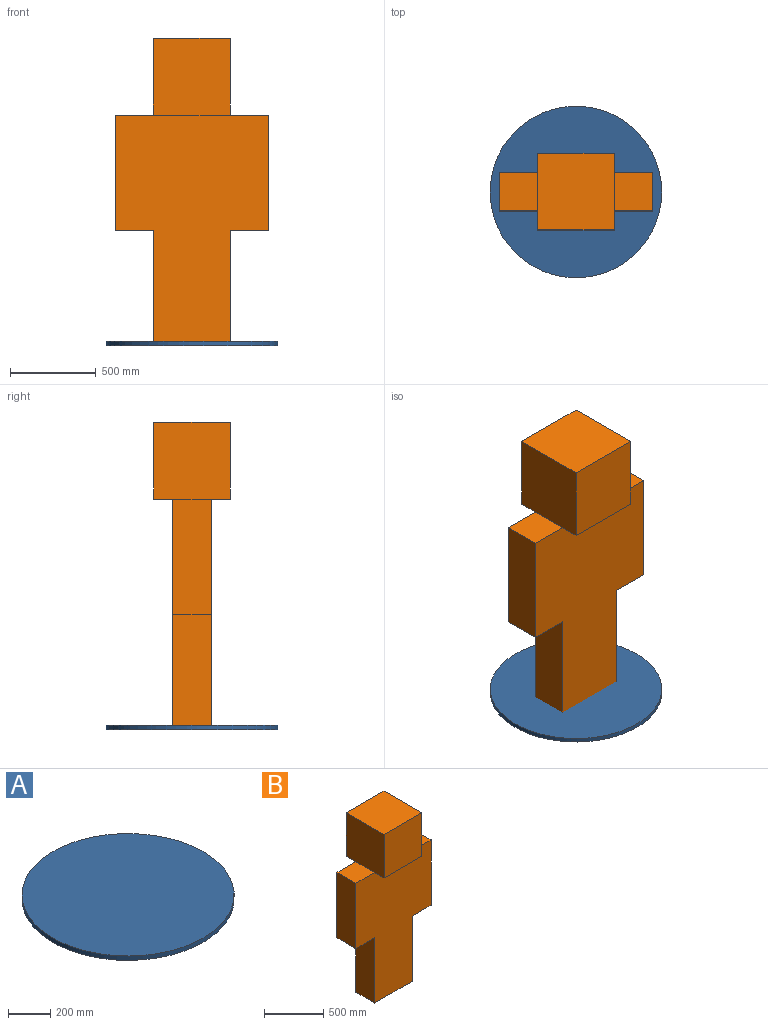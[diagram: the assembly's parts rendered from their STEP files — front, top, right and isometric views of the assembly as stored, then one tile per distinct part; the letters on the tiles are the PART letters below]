
ASSEMBLY  parts=2 mates=1
PART A: 3 faces, bbox 1000x1000x25 mm
  f0: cylinder r=500mm len=1000mm, axis (0,0,-1), area 78539.8mm2, adj f1,f2
  f1: plane 1000x1000mm, normal (0,0,1), area 785398.2mm2, adj f0
  f2: plane 1000x1000mm, normal (0,0,-1), area 785398.2mm2, adj f0
PART B: 18 faces, bbox 896x448x1792 mm
  f0: plane 224x224mm, normal (0,0,1), area 50176mm2, adj f1,f9,f10,f15
  f1: plane 672x224mm, normal (1,0,0), area 150528mm2, adj f0,f8,f9,f10
  f2: plane 224x224mm, normal (0,0,1), area 50176mm2, adj f3,f9,f10,f13
  f3: plane 672x224mm, normal (-1,0,0), area 150528mm2, adj f2,f4,f9,f10
  f4: plane 224x224mm, normal (0,0,-1), area 50176mm2, adj f3,f5,f9,f10
  f5: plane 672x224mm, normal (-1,0,0), area 150528mm2, adj f4,f6,f9,f10
  f6: plane 448x224mm, normal (0,0,-1), area 100352mm2, adj f5,f7,f9,f10
  f7: plane 672x224mm, normal (1,0,0), area 150528mm2, adj f6,f8,f9,f10
  f8: plane 224x224mm, normal (0,0,-1), area 50176mm2, adj f1,f7,f9,f10
  f9: plane 1344x896mm, normal (0,-1,0), area 903168mm2, adj f0,f1,f2,f3,f4,f5,f6,f7
  f10: plane 1344x896mm, normal (0,1,0), area 903168mm2, adj f0,f1,f2,f3,f4,f5,f6,f7
  f11: plane 448x112mm, normal (0,0,-1), area 50176mm2, adj f10,f13,f15,f17
  f12: plane 448x448mm, normal (0,0,1), area 200704mm2, adj f13,f15,f16,f17
  f13: plane 448x448mm, normal (-1,0,0), area 200704mm2, adj f2,f11,f12,f14,f16,f17
  f14: plane 448x112mm, normal (0,0,-1), area 50176mm2, adj f9,f13,f15,f16
  f15: plane 448x448mm, normal (1,0,0), area 200704mm2, adj f0,f11,f12,f14,f16,f17
  f16: plane 448x448mm, normal (0,-1,0), area 200704mm2, adj f12,f13,f14,f15
  f17: plane 448x448mm, normal (0,1,0), area 200704mm2, adj f11,f12,f13,f15
PLACE A at identity
PLACE B at identity
MATE fastened A.f0 <-> B.f6  axis (0,0,-1) through (448,-112,0)mm
